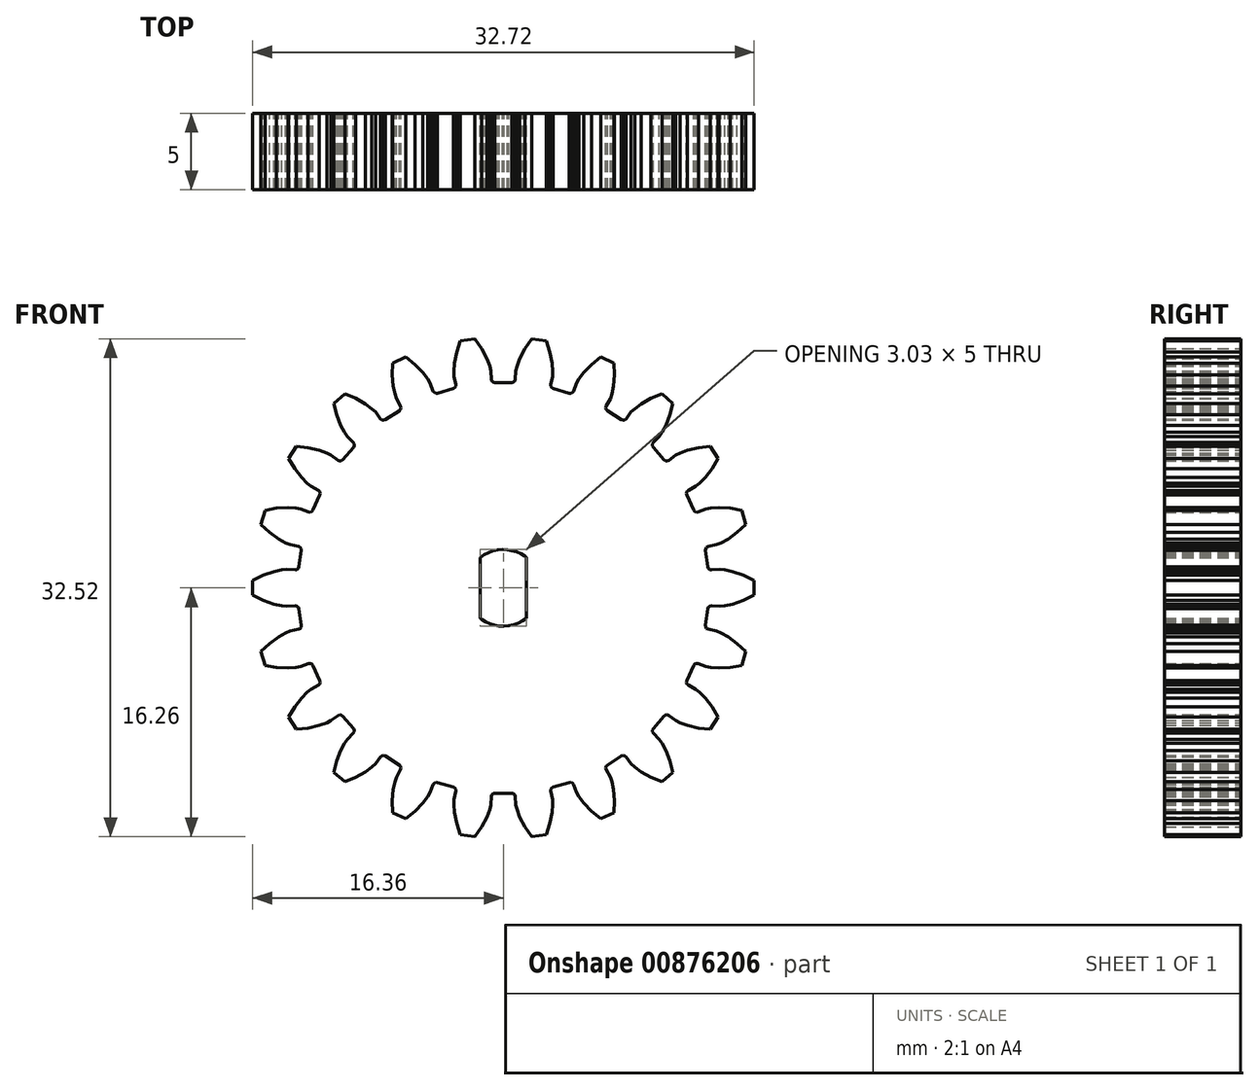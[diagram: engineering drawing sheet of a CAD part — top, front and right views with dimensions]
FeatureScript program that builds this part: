
annotation { "Feature Type Name" : "Feature", "Feature Type Description" : "" }
export const myFeature = defineFeature(function(context is Context, id is Id, definition is map)
    precondition{}
    {
        {
            var Q0;
            Q0=qCreatedBy(makeId("Front.planeOp"),FACE);
            var sketch = newSketch(context, id + "F0", { "sketchPlane" : qUnion([Q0])});
            skLineSegment(sketch, "E0", {"start": v(3.19, -14.67) * mm, "end": v(3.23, -14.15) * mm});
            skLineSegment(sketch, "E1", {"start": v(1.85, 16.26) * mm, "end": v(1.42, 15.62) * mm});
            skLineSegment(sketch, "E2", {"start": v(0.97, -2.3) * mm, "end": v(0.68, -2.4) * mm});
            skLineSegment(sketch, "E3", {"start": v(3.1, 13.28) * mm, "end": v(3.22, 13.83) * mm});
            skLineSegment(sketch, "E4", {"start": v(5.25, 14.06) * mm, "end": v(4.93, 13.65) * mm});
            skLineSegment(sketch, "E5", {"start": v(-9, -12.02) * mm, "end": v(-8.58, -11.7) * mm});
            skLineSegment(sketch, "E6", {"start": v(6.8, -11.58) * mm, "end": v(7.7, -10.99) * mm});
            skLineSegment(sketch, "E7", {"start": v(14.2, -2.94) * mm, "end": v(13.92, -2.82) * mm});
            skLineSegment(sketch, "E8", {"start": v(-0.54, 13.41) * mm, "end": v(-0.65, 13.44) * mm});
            skLineSegment(sketch, "E9", {"start": v(0.54, 13.41) * mm, "end": v(-0.54, 13.41) * mm});
            skLineSegment(sketch, "E10", {"start": v(-0.81, 14.18) * mm, "end": v(-0.89, 14.48) * mm});
            skLineSegment(sketch, "E11", {"start": v(-0.65, 13.44) * mm, "end": v(-0.74, 13.5) * mm});
            skLineSegment(sketch, "E12", {"start": v(-6.71, 11.66) * mm, "end": v(-6.8, 11.58) * mm});
            skLineSegment(sketch, "E13", {"start": v(0.81, 14.18) * mm, "end": v(0.77, 13.61) * mm});
            skLineSegment(sketch, "E14", {"start": v(-9.73, -9.3) * mm, "end": v(-9.73, -9.4) * mm});
            skLineSegment(sketch, "E15", {"start": v(3.1, 13.17) * mm, "end": v(3.1, 13.28) * mm});
            skLineSegment(sketch, "E16", {"start": v(-0.37, 2.47) * mm, "end": v(-0.06, 2.5) * mm});
            skLineSegment(sketch, "E17", {"start": v(0.68, -2.4) * mm, "end": v(0.37, -2.47) * mm});
            skLineSegment(sketch, "E18", {"start": v(4.57, 12.85) * mm, "end": v(4.51, 12.75) * mm});
            skLineSegment(sketch, "E19", {"start": v(0.89, 14.48) * mm, "end": v(0.81, 14.18) * mm});
            skLineSegment(sketch, "E20", {"start": v(1.25, -2.16) * mm, "end": v(0.97, -2.3) * mm});
            skLineSegment(sketch, "E21", {"start": v(-7.23, -14.68) * mm, "end": v(-6.36, -15.08) * mm});
            skLineSegment(sketch, "E22", {"start": v(-8.58, -11.7) * mm, "end": v(-8.35, -11.49) * mm});
            skLineSegment(sketch, "E23", {"start": v(-1.42, 15.62) * mm, "end": v(-1.85, 16.26) * mm});
            skLineSegment(sketch, "E24", {"start": v(0.37, -2.47) * mm, "end": v(0.06, -2.5) * mm});
            skLineSegment(sketch, "E25", {"start": v(-5.25, -14.06) * mm, "end": v(-4.93, -13.65) * mm});
            skLineSegment(sketch, "E26", {"start": v(3.04, 15.4) * mm, "end": v(2.8, 16.12) * mm});
            skLineSegment(sketch, "E27", {"start": v(-0.74, 13.5) * mm, "end": v(-0.77, 13.61) * mm});
            skLineSegment(sketch, "E28", {"start": v(14.07, -5.24) * mm, "end": v(14.8, -5.2) * mm});
            skLineSegment(sketch, "E29", {"start": v(-4.51, -12.75) * mm, "end": v(-4.41, -12.7) * mm});
            skLineSegment(sketch, "E30", {"start": v(-12.06, -6.36) * mm, "end": v(-12.56, -6.63) * mm});
            skLineSegment(sketch, "E31", {"start": v(-13.4, 1.27) * mm, "end": v(-13.48, 1.2) * mm});
            skLineSegment(sketch, "E32", {"start": v(-0.77, 13.61) * mm, "end": v(-0.81, 14.18) * mm});
            skLineSegment(sketch, "E33", {"start": v(-1.08, 14.97) * mm, "end": v(-1.42, 15.62) * mm});
            skLineSegment(sketch, "E34", {"start": v(-8, -11.04) * mm, "end": v(-7.92, -10.97) * mm});
            skLineSegment(sketch, "E35", {"start": v(-6.8, -11.58) * mm, "end": v(-6.71, -11.66) * mm});
            skLineSegment(sketch, "E36", {"start": v(-14.67, 3.2) * mm, "end": v(-14.2, 2.94) * mm});
            skLineSegment(sketch, "E37", {"start": v(-3.19, -14.67) * mm, "end": v(-3.04, -15.4) * mm});
            skLineSegment(sketch, "E38", {"start": v(0.54, -13.41) * mm, "end": v(0.65, -13.44) * mm});
            skLineSegment(sketch, "E39", {"start": v(-15.26, 3.63) * mm, "end": v(-14.67, 3.2) * mm});
            skLineSegment(sketch, "E40", {"start": v(-13.23, 5.15) * mm, "end": v(-13.54, 5.2) * mm});
            skLineSegment(sketch, "E41", {"start": v(-4.93, -13.65) * mm, "end": v(-4.77, -13.37) * mm});
            skLineSegment(sketch, "E42", {"start": v(-12.06, 6.36) * mm, "end": v(-11.98, 6.28) * mm});
            skLineSegment(sketch, "E43", {"start": v(-16.36, 0.48) * mm, "end": v(-16.36, -0.48) * mm});
            skLineSegment(sketch, "E44", {"start": v(-15.67, 0.82) * mm, "end": v(-16.36, 0.48) * mm});
            skLineSegment(sketch, "E45", {"start": v(3.19, 14.67) * mm, "end": v(3.04, 15.4) * mm});
            skLineSegment(sketch, "E46", {"start": v(3.23, 14.15) * mm, "end": v(3.19, 14.67) * mm});
            skLineSegment(sketch, "E47", {"start": v(3.22, 13.83) * mm, "end": v(3.23, 14.15) * mm});
            skLineSegment(sketch, "E48", {"start": v(0.26, 2.49) * mm, "end": v(0.57, 2.43) * mm});
            skLineSegment(sketch, "E49", {"start": v(-0.06, 2.5) * mm, "end": v(0.26, 2.49) * mm});
            skLineSegment(sketch, "E50", {"start": v(-14.02, -8.44) * mm, "end": v(-13.5, -9.25) * mm});
            skLineSegment(sketch, "E51", {"start": v(-13.62, -7.78) * mm, "end": v(-14.02, -8.44) * mm});
            skLineSegment(sketch, "E52", {"start": v(-0.68, 2.4) * mm, "end": v(-0.37, 2.47) * mm});
            skLineSegment(sketch, "E53", {"start": v(-3.16, 13.08) * mm, "end": v(-3.26, 13.02) * mm});
            skLineSegment(sketch, "E54", {"start": v(-3.1, 13.17) * mm, "end": v(-3.16, 13.08) * mm});
            skLineSegment(sketch, "E55", {"start": v(-3.1, 13.28) * mm, "end": v(-3.1, 13.17) * mm});
            skLineSegment(sketch, "E56", {"start": v(-3.22, 13.83) * mm, "end": v(-3.1, 13.28) * mm});
            skLineSegment(sketch, "E57", {"start": v(-3.23, 14.15) * mm, "end": v(-3.22, 13.83) * mm});
            skLineSegment(sketch, "E58", {"start": v(-3.19, 14.67) * mm, "end": v(-3.23, 14.15) * mm});
            skLineSegment(sketch, "E59", {"start": v(-3.04, 15.4) * mm, "end": v(-3.19, 14.67) * mm});
            skLineSegment(sketch, "E60", {"start": v(-2.8, 16.12) * mm, "end": v(-3.04, 15.4) * mm});
            skLineSegment(sketch, "E61", {"start": v(-1.85, 16.26) * mm, "end": v(-2.8, 16.12) * mm});
            skLineSegment(sketch, "E62", {"start": v(5.76, 14.6) * mm, "end": v(5.25, 14.06) * mm});
            skLineSegment(sketch, "E63", {"start": v(6.36, 15.08) * mm, "end": v(5.76, 14.6) * mm});
            skLineSegment(sketch, "E64", {"start": v(7.23, 14.68) * mm, "end": v(6.36, 15.08) * mm});
            skLineSegment(sketch, "E65", {"start": v(-7.2, 13.18) * mm, "end": v(-7.08, 12.66) * mm});
            skLineSegment(sketch, "E66", {"start": v(-7.25, 13.91) * mm, "end": v(-7.2, 13.18) * mm});
            skLineSegment(sketch, "E67", {"start": v(-7.23, 14.68) * mm, "end": v(-7.25, 13.91) * mm});
            skLineSegment(sketch, "E68", {"start": v(-6.36, 15.08) * mm, "end": v(-7.23, 14.68) * mm});
            skLineSegment(sketch, "E69", {"start": v(-5.76, 14.6) * mm, "end": v(-6.36, 15.08) * mm});
            skLineSegment(sketch, "E70", {"start": v(-5.25, 14.06) * mm, "end": v(-5.76, 14.6) * mm});
            skLineSegment(sketch, "E71", {"start": v(-4.93, 13.65) * mm, "end": v(-5.25, 14.06) * mm});
            skLineSegment(sketch, "E72", {"start": v(-4.77, 13.37) * mm, "end": v(-4.93, 13.65) * mm});
            skLineSegment(sketch, "E73", {"start": v(-4.57, 12.85) * mm, "end": v(-4.77, 13.37) * mm});
            skLineSegment(sketch, "E74", {"start": v(-4.51, 12.75) * mm, "end": v(-4.57, 12.85) * mm});
            skLineSegment(sketch, "E75", {"start": v(1.42, 15.62) * mm, "end": v(1.08, 14.97) * mm});
            skLineSegment(sketch, "E76", {"start": v(-13.54, 5.2) * mm, "end": v(-14.07, 5.24) * mm});
            skLineSegment(sketch, "E77", {"start": v(-0.89, 14.48) * mm, "end": v(-1.08, 14.97) * mm});
            skLineSegment(sketch, "E78", {"start": v(13.17, -7.2) * mm, "end": v(12.8, -6.82) * mm});
            skLineSegment(sketch, "E79", {"start": v(2.8, 16.12) * mm, "end": v(1.85, 16.26) * mm});
            skLineSegment(sketch, "E80", {"start": v(-2.8, -16.12) * mm, "end": v(-1.85, -16.26) * mm});
            skLineSegment(sketch, "E81", {"start": v(-11.97, -6.07) * mm, "end": v(-11.95, -6.17) * mm});
            skLineSegment(sketch, "E82", {"start": v(-6.71, -11.87) * mm, "end": v(-6.98, -12.36) * mm});
            skLineSegment(sketch, "E83", {"start": v(-14.46, 1.18) * mm, "end": v(-14.97, 1.07) * mm});
            skLineSegment(sketch, "E84", {"start": v(-14.07, 5.24) * mm, "end": v(-14.8, 5.2) * mm});
            skLineSegment(sketch, "E85", {"start": v(-1.85, -16.26) * mm, "end": v(-1.42, -15.62) * mm});
            skLineSegment(sketch, "E86", {"start": v(-6.36, -15.08) * mm, "end": v(-5.76, -14.6) * mm});
            skLineSegment(sketch, "E87", {"start": v(-4.3, -12.72) * mm, "end": v(-4.41, -12.7) * mm});
            skLineSegment(sketch, "E88", {"start": v(-7.7, -10.99) * mm, "end": v(-7.81, -10.95) * mm});
            skLineSegment(sketch, "E89", {"start": v(7.23, 14.68) * mm, "end": v(7.25, 13.91) * mm});
            skLineSegment(sketch, "E90", {"start": v(0.74, -13.5) * mm, "end": v(0.77, -13.61) * mm});
            skLineSegment(sketch, "E91", {"start": v(-15.56, 5.07) * mm, "end": v(-14.8, 5.2) * mm});
            skLineSegment(sketch, "E92", {"start": v(-3.22, -13.83) * mm, "end": v(-3.23, -14.15) * mm});
            skLineSegment(sketch, "E93", {"start": v(-15.56, 5.07) * mm, "end": v(-15.83, 4.15) * mm});
            skLineSegment(sketch, "E94", {"start": v(-12.8, -6.82) * mm, "end": v(-13.17, -7.2) * mm});
            skLineSegment(sketch, "E95", {"start": v(-13.23, 5.15) * mm, "end": v(-12.7, 4.96) * mm});
            skLineSegment(sketch, "E96", {"start": v(-5.25, -14.06) * mm, "end": v(-5.76, -14.6) * mm});
            skLineSegment(sketch, "E97", {"start": v(-15.26, 3.63) * mm, "end": v(-15.83, 4.15) * mm});
            skLineSegment(sketch, "E98", {"start": v(13.5, -9.25) * mm, "end": v(12.74, -9.16) * mm});
            skLineSegment(sketch, "E99", {"start": v(-13.2, -2.56) * mm, "end": v(-13.27, -2.65) * mm});
            skLineSegment(sketch, "E100", {"start": v(-12.8, -6.82) * mm, "end": v(-12.56, -6.63) * mm});
            skLineSegment(sketch, "E101", {"start": v(-13.48, -1.2) * mm, "end": v(-13.59, -1.18) * mm});
            skLineSegment(sketch, "E102", {"start": v(-3.16, -13.08) * mm, "end": v(-3.1, -13.17) * mm});
            skLineSegment(sketch, "E103", {"start": v(-0.89, -14.48) * mm, "end": v(-1.08, -14.97) * mm});
            skLineSegment(sketch, "E104", {"start": v(11.53, -8.81) * mm, "end": v(11.24, -8.67) * mm});
            skLineSegment(sketch, "E105", {"start": v(-12.02, -9) * mm, "end": v(-12.74, -9.16) * mm});
            skLineSegment(sketch, "E106", {"start": v(-7.81, -10.95) * mm, "end": v(-7.92, -10.97) * mm});
            skLineSegment(sketch, "E107", {"start": v(-0.54, -13.41) * mm, "end": v(-0.65, -13.44) * mm});
            skLineSegment(sketch, "E108", {"start": v(9.64, -12.38) * mm, "end": v(9, -12.02) * mm});
            skLineSegment(sketch, "E109", {"start": v(-3.1, -13.28) * mm, "end": v(-3.22, -13.83) * mm});
            skLineSegment(sketch, "E110", {"start": v(-3.04, -15.4) * mm, "end": v(-2.8, -16.12) * mm});
            skLineSegment(sketch, "E111", {"start": v(-1.5, -2) * mm, "end": v(-1.51, 1.99) * mm});
            skLineSegment(sketch, "E112", {"start": v(-1.42, -2.05) * mm, "end": v(-1.5, -2) * mm});
            skLineSegment(sketch, "E113", {"start": v(-1.16, -2.22) * mm, "end": v(-1.42, -2.05) * mm});
            skLineSegment(sketch, "E114", {"start": v(-1.42, -15.62) * mm, "end": v(-1.08, -14.97) * mm});
            skLineSegment(sketch, "E115", {"start": v(-0.87, -2.34) * mm, "end": v(-1.16, -2.22) * mm});
            skLineSegment(sketch, "E116", {"start": v(-0.89, -14.48) * mm, "end": v(-0.81, -14.18) * mm});
            skLineSegment(sketch, "E117", {"start": v(-0.57, -2.43) * mm, "end": v(-0.87, -2.34) * mm});
            skLineSegment(sketch, "E118", {"start": v(-0.81, -14.18) * mm, "end": v(-0.77, -13.61) * mm});
            skLineSegment(sketch, "E119", {"start": v(-0.77, -13.61) * mm, "end": v(-0.74, -13.5) * mm});
            skLineSegment(sketch, "E120", {"start": v(-0.74, -13.5) * mm, "end": v(-0.65, -13.44) * mm});
            skLineSegment(sketch, "E121", {"start": v(-0.26, -2.49) * mm, "end": v(-0.57, -2.43) * mm});
            skLineSegment(sketch, "E122", {"start": v(-0.54, -13.41) * mm, "end": v(0.54, -13.41) * mm});
            skLineSegment(sketch, "E123", {"start": v(0.06, -2.5) * mm, "end": v(-0.26, -2.49) * mm});
            skLineSegment(sketch, "E124", {"start": v(0.65, -13.44) * mm, "end": v(0.74, -13.5) * mm});
            skLineSegment(sketch, "E125", {"start": v(0.77, -13.61) * mm, "end": v(0.81, -14.18) * mm});
            skLineSegment(sketch, "E126", {"start": v(0.81, -14.18) * mm, "end": v(0.89, -14.48) * mm});
            skLineSegment(sketch, "E127", {"start": v(0.89, -14.48) * mm, "end": v(1.08, -14.97) * mm});
            skLineSegment(sketch, "E128", {"start": v(1.08, -14.97) * mm, "end": v(1.42, -15.62) * mm});
            skLineSegment(sketch, "E129", {"start": v(1.51, -1.99) * mm, "end": v(1.25, -2.16) * mm});
            skLineSegment(sketch, "E130", {"start": v(1.42, -15.62) * mm, "end": v(1.85, -16.26) * mm});
            skLineSegment(sketch, "E131", {"start": v(-15.26, -3.63) * mm, "end": v(-15.83, -4.15) * mm});
            skLineSegment(sketch, "E132", {"start": v(-15.83, -4.15) * mm, "end": v(-15.56, -5.07) * mm});
            skLineSegment(sketch, "E133", {"start": v(-15.56, -5.07) * mm, "end": v(-14.8, -5.2) * mm});
            skLineSegment(sketch, "E134", {"start": v(-14.67, -3.2) * mm, "end": v(-15.26, -3.63) * mm});
            skLineSegment(sketch, "E135", {"start": v(-14.8, -5.2) * mm, "end": v(-14.07, -5.24) * mm});
            skLineSegment(sketch, "E136", {"start": v(-14.2, -2.94) * mm, "end": v(-14.67, -3.2) * mm});
            skLineSegment(sketch, "E137", {"start": v(-13.92, -2.82) * mm, "end": v(-14.2, -2.94) * mm});
            skLineSegment(sketch, "E138", {"start": v(-14.07, -5.24) * mm, "end": v(-13.54, -5.2) * mm});
            skLineSegment(sketch, "E139", {"start": v(-13.37, -2.7) * mm, "end": v(-13.92, -2.82) * mm});
            skLineSegment(sketch, "E140", {"start": v(-13.54, -5.2) * mm, "end": v(-13.23, -5.15) * mm});
            skLineSegment(sketch, "E141", {"start": v(-13.27, -2.65) * mm, "end": v(-13.37, -2.7) * mm});
            skLineSegment(sketch, "E142", {"start": v(-13.23, -5.15) * mm, "end": v(-12.7, -4.96) * mm});
            skLineSegment(sketch, "E143", {"start": v(-13.2, -2.45) * mm, "end": v(-13.2, -2.56) * mm});
            skLineSegment(sketch, "E144", {"start": v(-13.17, -7.2) * mm, "end": v(-13.62, -7.78) * mm});
            skLineSegment(sketch, "E145", {"start": v(-13.5, -9.25) * mm, "end": v(-12.74, -9.16) * mm});
            skLineSegment(sketch, "E146", {"start": v(-11.98, -6.28) * mm, "end": v(-12.06, -6.36) * mm});
            skLineSegment(sketch, "E147", {"start": v(-12.02, -9) * mm, "end": v(-11.53, -8.81) * mm});
            skLineSegment(sketch, "E148", {"start": v(-11.95, -6.17) * mm, "end": v(-11.98, -6.28) * mm});
            skLineSegment(sketch, "E149", {"start": v(-10.88, -11.3) * mm, "end": v(-11.08, -12.05) * mm});
            skLineSegment(sketch, "E150", {"start": v(-11.08, -12.05) * mm, "end": v(-10.35, -12.68) * mm});
            skLineSegment(sketch, "E151", {"start": v(-10.61, -10.62) * mm, "end": v(-10.88, -11.3) * mm});
            skLineSegment(sketch, "E152", {"start": v(-10.36, -10.15) * mm, "end": v(-10.61, -10.62) * mm});
            skLineSegment(sketch, "E153", {"start": v(-10.18, -9.9) * mm, "end": v(-10.36, -10.15) * mm});
            skLineSegment(sketch, "E154", {"start": v(-10.35, -12.68) * mm, "end": v(-9.64, -12.38) * mm});
            skLineSegment(sketch, "E155", {"start": v(-9.79, -9.5) * mm, "end": v(-10.18, -9.9) * mm});
            skLineSegment(sketch, "E156", {"start": v(-9.73, -9.4) * mm, "end": v(-9.79, -9.5) * mm});
            skLineSegment(sketch, "E157", {"start": v(-7.2, -13.18) * mm, "end": v(-7.25, -13.91) * mm});
            skLineSegment(sketch, "E158", {"start": v(-7.25, -13.91) * mm, "end": v(-7.23, -14.68) * mm});
            skLineSegment(sketch, "E159", {"start": v(-7.08, -12.66) * mm, "end": v(-7.2, -13.18) * mm});
            skLineSegment(sketch, "E160", {"start": v(-6.98, -12.36) * mm, "end": v(-7.08, -12.66) * mm});
            skLineSegment(sketch, "E161", {"start": v(-6.69, -11.76) * mm, "end": v(-6.71, -11.87) * mm});
            skLineSegment(sketch, "E162", {"start": v(-3.23, -14.15) * mm, "end": v(-3.19, -14.67) * mm});
            skLineSegment(sketch, "E163", {"start": v(-7.08, 12.66) * mm, "end": v(-6.98, 12.36) * mm});
            skLineSegment(sketch, "E164", {"start": v(-6.98, 12.36) * mm, "end": v(-6.71, 11.87) * mm});
            skLineSegment(sketch, "E165", {"start": v(-6.71, 11.87) * mm, "end": v(-6.69, 11.76) * mm});
            skLineSegment(sketch, "E166", {"start": v(-4.77, -13.37) * mm, "end": v(-4.57, -12.85) * mm});
            skLineSegment(sketch, "E167", {"start": v(-4.57, -12.85) * mm, "end": v(-4.51, -12.75) * mm});
            skLineSegment(sketch, "E168", {"start": v(-4.41, 12.7) * mm, "end": v(-4.51, 12.75) * mm});
            skLineSegment(sketch, "E169", {"start": v(-4.3, 12.72) * mm, "end": v(-4.41, 12.7) * mm});
            skLineSegment(sketch, "E170", {"start": v(-4.3, -12.72) * mm, "end": v(-3.26, -13.02) * mm});
            skLineSegment(sketch, "E171", {"start": v(-3.26, 13.02) * mm, "end": v(-4.3, 12.72) * mm});
            skLineSegment(sketch, "E172", {"start": v(-3.26, -13.02) * mm, "end": v(-3.16, -13.08) * mm});
            skLineSegment(sketch, "E173", {"start": v(-3.1, -13.17) * mm, "end": v(-3.1, -13.28) * mm});
            skLineSegment(sketch, "E174", {"start": v(-10.35, 12.68) * mm, "end": v(-11.08, 12.05) * mm});
            skLineSegment(sketch, "E175", {"start": v(-11.08, 12.05) * mm, "end": v(-10.88, 11.3) * mm});
            skLineSegment(sketch, "E176", {"start": v(-10.88, 11.3) * mm, "end": v(-10.61, 10.62) * mm});
            skLineSegment(sketch, "E177", {"start": v(-10.61, 10.62) * mm, "end": v(-10.36, 10.15) * mm});
            skLineSegment(sketch, "E178", {"start": v(-10.36, 10.15) * mm, "end": v(-10.18, 9.9) * mm});
            skLineSegment(sketch, "E179", {"start": v(-9.64, 12.38) * mm, "end": v(-10.35, 12.68) * mm});
            skLineSegment(sketch, "E180", {"start": v(-10.18, 9.9) * mm, "end": v(-9.79, 9.5) * mm});
            skLineSegment(sketch, "E181", {"start": v(-9.79, 9.5) * mm, "end": v(-9.73, 9.4) * mm});
            skLineSegment(sketch, "E182", {"start": v(-9.73, 9.4) * mm, "end": v(-9.73, 9.3) * mm});
            skLineSegment(sketch, "E183", {"start": v(-9.64, -12.38) * mm, "end": v(-9, -12.02) * mm});
            skLineSegment(sketch, "E184", {"start": v(-9, 12.02) * mm, "end": v(-9.64, 12.38) * mm});
            skLineSegment(sketch, "E185", {"start": v(-8.58, 11.7) * mm, "end": v(-9, 12.02) * mm});
            skLineSegment(sketch, "E186", {"start": v(-8.35, 11.49) * mm, "end": v(-8.58, 11.7) * mm});
            skLineSegment(sketch, "E187", {"start": v(-8.35, -11.49) * mm, "end": v(-8, -11.04) * mm});
            skLineSegment(sketch, "E188", {"start": v(-8, 11.04) * mm, "end": v(-8.35, 11.49) * mm});
            skLineSegment(sketch, "E189", {"start": v(-7.92, 10.97) * mm, "end": v(-8, 11.04) * mm});
            skLineSegment(sketch, "E190", {"start": v(-7.81, 10.95) * mm, "end": v(-7.92, 10.97) * mm});
            skLineSegment(sketch, "E191", {"start": v(-7.7, 10.99) * mm, "end": v(-7.81, 10.95) * mm});
            skLineSegment(sketch, "E192", {"start": v(-7.7, -10.99) * mm, "end": v(-6.8, -11.58) * mm});
            skLineSegment(sketch, "E193", {"start": v(-6.8, 11.58) * mm, "end": v(-7.7, 10.99) * mm});
            skLineSegment(sketch, "E194", {"start": v(-6.71, -11.66) * mm, "end": v(-6.69, -11.76) * mm});
            skLineSegment(sketch, "E195", {"start": v(-6.69, 11.76) * mm, "end": v(-6.71, 11.66) * mm});
            skLineSegment(sketch, "E196", {"start": v(-13.5, 9.25) * mm, "end": v(-14.02, 8.44) * mm});
            skLineSegment(sketch, "E197", {"start": v(-14.02, 8.44) * mm, "end": v(-13.62, 7.78) * mm});
            skLineSegment(sketch, "E198", {"start": v(-13.62, 7.78) * mm, "end": v(-13.17, 7.2) * mm});
            skLineSegment(sketch, "E199", {"start": v(-12.74, 9.16) * mm, "end": v(-13.5, 9.25) * mm});
            skLineSegment(sketch, "E200", {"start": v(-13.17, 7.2) * mm, "end": v(-12.8, 6.82) * mm});
            skLineSegment(sketch, "E201", {"start": v(-12.8, 6.82) * mm, "end": v(-12.56, 6.63) * mm});
            skLineSegment(sketch, "E202", {"start": v(-12.02, 9) * mm, "end": v(-12.74, 9.16) * mm});
            skLineSegment(sketch, "E203", {"start": v(-12.56, 6.63) * mm, "end": v(-12.06, 6.36) * mm});
            skLineSegment(sketch, "E204", {"start": v(-11.53, 8.81) * mm, "end": v(-12.02, 9) * mm});
            skLineSegment(sketch, "E205", {"start": v(-11.98, 6.28) * mm, "end": v(-11.95, 6.17) * mm});
            skLineSegment(sketch, "E206", {"start": v(-11.53, -8.81) * mm, "end": v(-11.24, -8.67) * mm});
            skLineSegment(sketch, "E207", {"start": v(-11.24, 8.67) * mm, "end": v(-11.53, 8.81) * mm});
            skLineSegment(sketch, "E208", {"start": v(-11.24, -8.67) * mm, "end": v(-10.8, -8.33) * mm});
            skLineSegment(sketch, "E209", {"start": v(-10.8, 8.33) * mm, "end": v(-11.24, 8.67) * mm});
            skLineSegment(sketch, "E210", {"start": v(-10.8, -8.33) * mm, "end": v(-10.7, -8.3) * mm});
            skLineSegment(sketch, "E211", {"start": v(-10.7, 8.3) * mm, "end": v(-10.8, 8.33) * mm});
            skLineSegment(sketch, "E212", {"start": v(-10.7, -8.3) * mm, "end": v(-10.58, -8.3) * mm});
            skLineSegment(sketch, "E213", {"start": v(-10.58, 8.3) * mm, "end": v(-10.7, 8.3) * mm});
            skLineSegment(sketch, "E214", {"start": v(-10.58, -8.3) * mm, "end": v(-10.5, -8.37) * mm});
            skLineSegment(sketch, "E215", {"start": v(-10.5, 8.37) * mm, "end": v(-10.58, 8.3) * mm});
            skLineSegment(sketch, "E216", {"start": v(-10.5, -8.37) * mm, "end": v(-9.78, -9.2) * mm});
            skLineSegment(sketch, "E217", {"start": v(-9.78, 9.2) * mm, "end": v(-10.5, 8.37) * mm});
            skLineSegment(sketch, "E218", {"start": v(-9.78, -9.2) * mm, "end": v(-9.73, -9.3) * mm});
            skLineSegment(sketch, "E219", {"start": v(-9.73, 9.3) * mm, "end": v(-9.78, 9.2) * mm});
            skLineSegment(sketch, "E220", {"start": v(-14.2, 2.94) * mm, "end": v(-13.92, 2.82) * mm});
            skLineSegment(sketch, "E221", {"start": v(-13.92, 2.82) * mm, "end": v(-13.37, 2.7) * mm});
            skLineSegment(sketch, "E222", {"start": v(-13.37, 2.7) * mm, "end": v(-13.27, 2.65) * mm});
            skLineSegment(sketch, "E223", {"start": v(-13.27, 2.65) * mm, "end": v(-13.2, 2.56) * mm});
            skLineSegment(sketch, "E224", {"start": v(-13.2, 2.56) * mm, "end": v(-13.2, 2.45) * mm});
            skLineSegment(sketch, "E225", {"start": v(-12.7, -4.96) * mm, "end": v(-12.6, -4.94) * mm});
            skLineSegment(sketch, "E226", {"start": v(-12.6, 4.94) * mm, "end": v(-12.7, 4.96) * mm});
            skLineSegment(sketch, "E227", {"start": v(-12.6, -4.94) * mm, "end": v(-12.5, -4.99) * mm});
            skLineSegment(sketch, "E228", {"start": v(-12.5, 4.99) * mm, "end": v(-12.6, 4.94) * mm});
            skLineSegment(sketch, "E229", {"start": v(-12.5, -4.99) * mm, "end": v(-12.43, -5.08) * mm});
            skLineSegment(sketch, "E230", {"start": v(-12.43, 5.08) * mm, "end": v(-12.5, 4.99) * mm});
            skLineSegment(sketch, "E231", {"start": v(-12.43, -5.08) * mm, "end": v(-11.97, -6.07) * mm});
            skLineSegment(sketch, "E232", {"start": v(-11.97, 6.07) * mm, "end": v(-12.43, 5.08) * mm});
            skLineSegment(sketch, "E233", {"start": v(-11.95, 6.17) * mm, "end": v(-11.97, 6.07) * mm});
            skLineSegment(sketch, "E234", {"start": v(-16.36, -0.48) * mm, "end": v(-15.67, -0.82) * mm});
            skLineSegment(sketch, "E235", {"start": v(-15.67, -0.82) * mm, "end": v(-14.97, -1.07) * mm});
            skLineSegment(sketch, "E236", {"start": v(-14.97, 1.07) * mm, "end": v(-15.67, 0.82) * mm});
            skLineSegment(sketch, "E237", {"start": v(-14.97, -1.07) * mm, "end": v(-14.46, -1.18) * mm});
            skLineSegment(sketch, "E238", {"start": v(-14.46, -1.18) * mm, "end": v(-14.15, -1.22) * mm});
            skLineSegment(sketch, "E239", {"start": v(-14.15, 1.22) * mm, "end": v(-14.46, 1.18) * mm});
            skLineSegment(sketch, "E240", {"start": v(-14.15, -1.22) * mm, "end": v(-13.59, -1.18) * mm});
            skLineSegment(sketch, "E241", {"start": v(-13.59, 1.18) * mm, "end": v(-14.15, 1.22) * mm});
            skLineSegment(sketch, "E242", {"start": v(-13.48, 1.2) * mm, "end": v(-13.59, 1.18) * mm});
            skLineSegment(sketch, "E243", {"start": v(-13.48, -1.2) * mm, "end": v(-13.4, -1.27) * mm});
            skLineSegment(sketch, "E244", {"start": v(-13.4, -1.27) * mm, "end": v(-13.35, -1.37) * mm});
            skLineSegment(sketch, "E245", {"start": v(-13.35, 1.37) * mm, "end": v(-13.4, 1.27) * mm});
            skLineSegment(sketch, "E246", {"start": v(-13.35, -1.37) * mm, "end": v(-13.2, -2.45) * mm});
            skLineSegment(sketch, "E247", {"start": v(-13.2, 2.45) * mm, "end": v(-13.35, 1.37) * mm});
            skLineSegment(sketch, "E248", {"start": v(-1.51, 1.99) * mm, "end": v(-1.25, 2.16) * mm});
            skLineSegment(sketch, "E249", {"start": v(-1.25, 2.16) * mm, "end": v(-0.97, 2.3) * mm});
            skLineSegment(sketch, "E250", {"start": v(-0.97, 2.3) * mm, "end": v(-0.68, 2.4) * mm});
            skLineSegment(sketch, "E251", {"start": v(0.65, 13.44) * mm, "end": v(0.54, 13.41) * mm});
            skLineSegment(sketch, "E252", {"start": v(0.57, 2.43) * mm, "end": v(0.87, 2.34) * mm});
            skLineSegment(sketch, "E253", {"start": v(0.74, 13.5) * mm, "end": v(0.65, 13.44) * mm});
            skLineSegment(sketch, "E254", {"start": v(0.77, 13.61) * mm, "end": v(0.74, 13.5) * mm});
            skLineSegment(sketch, "E255", {"start": v(0.87, 2.34) * mm, "end": v(1.16, 2.22) * mm});
            skLineSegment(sketch, "E256", {"start": v(1.08, 14.97) * mm, "end": v(0.89, 14.48) * mm});
            skLineSegment(sketch, "E257", {"start": v(1.16, 2.22) * mm, "end": v(1.42, 2.05) * mm});
            skLineSegment(sketch, "E258", {"start": v(1.42, 2.05) * mm, "end": v(1.5, 2) * mm});
            skLineSegment(sketch, "E259", {"start": v(1.5, 2) * mm, "end": v(1.51, -1.99) * mm});
            skLineSegment(sketch, "E260", {"start": v(1.85, -16.26) * mm, "end": v(2.8, -16.12) * mm});
            skLineSegment(sketch, "E261", {"start": v(2.8, -16.12) * mm, "end": v(3.04, -15.4) * mm});
            skLineSegment(sketch, "E262", {"start": v(3.04, -15.4) * mm, "end": v(3.19, -14.67) * mm});
            skLineSegment(sketch, "E263", {"start": v(3.22, -13.83) * mm, "end": v(3.1, -13.28) * mm});
            skLineSegment(sketch, "E264", {"start": v(3.23, -14.15) * mm, "end": v(3.22, -13.83) * mm});
            skLineSegment(sketch, "E265", {"start": v(3.1, -13.28) * mm, "end": v(3.1, -13.17) * mm});
            skLineSegment(sketch, "E266", {"start": v(3.1, -13.17) * mm, "end": v(3.16, -13.08) * mm});
            skLineSegment(sketch, "E267", {"start": v(3.16, 13.08) * mm, "end": v(3.1, 13.17) * mm});
            skLineSegment(sketch, "E268", {"start": v(3.16, -13.08) * mm, "end": v(3.26, -13.02) * mm});
            skLineSegment(sketch, "E269", {"start": v(3.26, 13.02) * mm, "end": v(3.16, 13.08) * mm});
            skLineSegment(sketch, "E270", {"start": v(3.26, -13.02) * mm, "end": v(4.3, -12.72) * mm});
            skLineSegment(sketch, "E271", {"start": v(4.3, 12.72) * mm, "end": v(3.26, 13.02) * mm});
            skLineSegment(sketch, "E272", {"start": v(4.3, -12.72) * mm, "end": v(4.41, -12.7) * mm});
            skLineSegment(sketch, "E273", {"start": v(4.41, 12.7) * mm, "end": v(4.3, 12.72) * mm});
            skLineSegment(sketch, "E274", {"start": v(4.41, -12.7) * mm, "end": v(4.51, -12.75) * mm});
            skLineSegment(sketch, "E275", {"start": v(4.51, 12.75) * mm, "end": v(4.41, 12.7) * mm});
            skLineSegment(sketch, "E276", {"start": v(4.51, -12.75) * mm, "end": v(4.57, -12.85) * mm});
            skLineSegment(sketch, "E277", {"start": v(4.57, -12.85) * mm, "end": v(4.77, -13.37) * mm});
            skLineSegment(sketch, "E278", {"start": v(4.77, 13.37) * mm, "end": v(4.57, 12.85) * mm});
            skLineSegment(sketch, "E279", {"start": v(4.77, -13.37) * mm, "end": v(4.93, -13.65) * mm});
            skLineSegment(sketch, "E280", {"start": v(4.93, 13.65) * mm, "end": v(4.77, 13.37) * mm});
            skLineSegment(sketch, "E281", {"start": v(4.93, -13.65) * mm, "end": v(5.25, -14.06) * mm});
            skLineSegment(sketch, "E282", {"start": v(5.25, -14.06) * mm, "end": v(5.76, -14.6) * mm});
            skLineSegment(sketch, "E283", {"start": v(5.76, -14.6) * mm, "end": v(6.36, -15.08) * mm});
            skLineSegment(sketch, "E284", {"start": v(6.36, -15.08) * mm, "end": v(7.23, -14.68) * mm});
            skLineSegment(sketch, "E285", {"start": v(6.71, -11.87) * mm, "end": v(6.69, -11.76) * mm});
            skLineSegment(sketch, "E286", {"start": v(6.98, -12.36) * mm, "end": v(6.71, -11.87) * mm});
            skLineSegment(sketch, "E287", {"start": v(7.08, -12.66) * mm, "end": v(6.98, -12.36) * mm});
            skLineSegment(sketch, "E288", {"start": v(7.2, -13.18) * mm, "end": v(7.08, -12.66) * mm});
            skLineSegment(sketch, "E289", {"start": v(7.23, -14.68) * mm, "end": v(7.25, -13.91) * mm});
            skLineSegment(sketch, "E290", {"start": v(7.25, -13.91) * mm, "end": v(7.2, -13.18) * mm});
            skLineSegment(sketch, "E291", {"start": v(6.69, -11.76) * mm, "end": v(6.71, -11.66) * mm});
            skLineSegment(sketch, "E292", {"start": v(6.71, 11.66) * mm, "end": v(6.69, 11.76) * mm});
            skLineSegment(sketch, "E293", {"start": v(6.71, -11.66) * mm, "end": v(6.8, -11.58) * mm});
            skLineSegment(sketch, "E294", {"start": v(6.8, 11.58) * mm, "end": v(6.71, 11.66) * mm});
            skLineSegment(sketch, "E295", {"start": v(7.7, 10.99) * mm, "end": v(6.8, 11.58) * mm});
            skLineSegment(sketch, "E296", {"start": v(7.7, -10.99) * mm, "end": v(7.81, -10.95) * mm});
            skLineSegment(sketch, "E297", {"start": v(7.81, 10.95) * mm, "end": v(7.7, 10.99) * mm});
            skLineSegment(sketch, "E298", {"start": v(7.81, -10.95) * mm, "end": v(7.92, -10.97) * mm});
            skLineSegment(sketch, "E299", {"start": v(7.92, 10.97) * mm, "end": v(7.81, 10.95) * mm});
            skLineSegment(sketch, "E300", {"start": v(7.92, -10.97) * mm, "end": v(8, -11.04) * mm});
            skLineSegment(sketch, "E301", {"start": v(8, 11.04) * mm, "end": v(7.92, 10.97) * mm});
            skLineSegment(sketch, "E302", {"start": v(8, -11.04) * mm, "end": v(8.35, -11.49) * mm});
            skLineSegment(sketch, "E303", {"start": v(8.35, 11.49) * mm, "end": v(8, 11.04) * mm});
            skLineSegment(sketch, "E304", {"start": v(8.35, -11.49) * mm, "end": v(8.58, -11.7) * mm});
            skLineSegment(sketch, "E305", {"start": v(8.58, 11.7) * mm, "end": v(8.35, 11.49) * mm});
            skLineSegment(sketch, "E306", {"start": v(8.58, -11.7) * mm, "end": v(9, -12.02) * mm});
            skLineSegment(sketch, "E307", {"start": v(9, 12.02) * mm, "end": v(8.58, 11.7) * mm});
            skLineSegment(sketch, "E308", {"start": v(9.64, 12.38) * mm, "end": v(9, 12.02) * mm});
            skLineSegment(sketch, "E309", {"start": v(9.73, -9.4) * mm, "end": v(9.73, -9.3) * mm});
            skLineSegment(sketch, "E310", {"start": v(9.64, -12.38) * mm, "end": v(10.35, -12.68) * mm});
            skLineSegment(sketch, "E311", {"start": v(9.79, -9.5) * mm, "end": v(9.73, -9.4) * mm});
            skLineSegment(sketch, "E312", {"start": v(10.18, -9.9) * mm, "end": v(9.79, -9.5) * mm});
            skLineSegment(sketch, "E313", {"start": v(10.36, -10.15) * mm, "end": v(10.18, -9.9) * mm});
            skLineSegment(sketch, "E314", {"start": v(10.35, -12.68) * mm, "end": v(11.08, -12.05) * mm});
            skLineSegment(sketch, "E315", {"start": v(10.61, -10.62) * mm, "end": v(10.36, -10.15) * mm});
            skLineSegment(sketch, "E316", {"start": v(11.08, -12.05) * mm, "end": v(10.88, -11.3) * mm});
            skLineSegment(sketch, "E317", {"start": v(10.88, -11.3) * mm, "end": v(10.61, -10.62) * mm});
            skLineSegment(sketch, "E318", {"start": v(9.73, -9.3) * mm, "end": v(9.78, -9.2) * mm});
            skLineSegment(sketch, "E319", {"start": v(9.78, 9.2) * mm, "end": v(9.73, 9.3) * mm});
            skLineSegment(sketch, "E320", {"start": v(9.78, -9.2) * mm, "end": v(10.5, -8.37) * mm});
            skLineSegment(sketch, "E321", {"start": v(10.5, 8.37) * mm, "end": v(9.78, 9.2) * mm});
            skLineSegment(sketch, "E322", {"start": v(10.5, -8.37) * mm, "end": v(10.58, -8.3) * mm});
            skLineSegment(sketch, "E323", {"start": v(10.58, 8.3) * mm, "end": v(10.5, 8.37) * mm});
            skLineSegment(sketch, "E324", {"start": v(10.58, -8.3) * mm, "end": v(10.7, -8.3) * mm});
            skLineSegment(sketch, "E325", {"start": v(10.7, 8.3) * mm, "end": v(10.58, 8.3) * mm});
            skLineSegment(sketch, "E326", {"start": v(10.7, -8.3) * mm, "end": v(10.8, -8.33) * mm});
            skLineSegment(sketch, "E327", {"start": v(10.8, 8.33) * mm, "end": v(10.7, 8.3) * mm});
            skLineSegment(sketch, "E328", {"start": v(10.8, -8.33) * mm, "end": v(11.24, -8.67) * mm});
            skLineSegment(sketch, "E329", {"start": v(11.24, 8.67) * mm, "end": v(10.8, 8.33) * mm});
            skLineSegment(sketch, "E330", {"start": v(11.53, 8.81) * mm, "end": v(11.24, 8.67) * mm});
            skLineSegment(sketch, "E331", {"start": v(11.53, -8.81) * mm, "end": v(12.02, -9) * mm});
            skLineSegment(sketch, "E332", {"start": v(11.98, -6.28) * mm, "end": v(11.95, -6.17) * mm});
            skLineSegment(sketch, "E333", {"start": v(12.06, -6.36) * mm, "end": v(11.98, -6.28) * mm});
            skLineSegment(sketch, "E334", {"start": v(12.02, -9) * mm, "end": v(12.74, -9.16) * mm});
            skLineSegment(sketch, "E335", {"start": v(12.56, -6.63) * mm, "end": v(12.06, -6.36) * mm});
            skLineSegment(sketch, "E336", {"start": v(12.8, -6.82) * mm, "end": v(12.56, -6.63) * mm});
            skLineSegment(sketch, "E337", {"start": v(13.62, -7.78) * mm, "end": v(13.17, -7.2) * mm});
            skLineSegment(sketch, "E338", {"start": v(13.5, -9.25) * mm, "end": v(14.02, -8.44) * mm});
            skLineSegment(sketch, "E339", {"start": v(14.02, -8.44) * mm, "end": v(13.62, -7.78) * mm});
            skLineSegment(sketch, "E340", {"start": v(11.95, -6.17) * mm, "end": v(11.97, -6.07) * mm});
            skLineSegment(sketch, "E341", {"start": v(11.97, 6.07) * mm, "end": v(11.95, 6.17) * mm});
            skLineSegment(sketch, "E342", {"start": v(11.97, -6.07) * mm, "end": v(12.43, -5.08) * mm});
            skLineSegment(sketch, "E343", {"start": v(12.43, 5.08) * mm, "end": v(11.97, 6.07) * mm});
            skLineSegment(sketch, "E344", {"start": v(12.43, -5.08) * mm, "end": v(12.5, -4.99) * mm});
            skLineSegment(sketch, "E345", {"start": v(12.5, 4.99) * mm, "end": v(12.43, 5.08) * mm});
            skLineSegment(sketch, "E346", {"start": v(12.5, -4.99) * mm, "end": v(12.6, -4.94) * mm});
            skLineSegment(sketch, "E347", {"start": v(12.6, 4.94) * mm, "end": v(12.5, 4.99) * mm});
            skLineSegment(sketch, "E348", {"start": v(12.6, -4.94) * mm, "end": v(12.7, -4.96) * mm});
            skLineSegment(sketch, "E349", {"start": v(12.7, 4.96) * mm, "end": v(12.6, 4.94) * mm});
            skLineSegment(sketch, "E350", {"start": v(12.7, -4.96) * mm, "end": v(13.23, -5.15) * mm});
            skLineSegment(sketch, "E351", {"start": v(13.2, -2.56) * mm, "end": v(13.2, -2.45) * mm});
            skLineSegment(sketch, "E352", {"start": v(13.27, -2.65) * mm, "end": v(13.2, -2.56) * mm});
            skLineSegment(sketch, "E353", {"start": v(13.23, -5.15) * mm, "end": v(13.54, -5.2) * mm});
            skLineSegment(sketch, "E354", {"start": v(13.37, -2.7) * mm, "end": v(13.27, -2.65) * mm});
            skLineSegment(sketch, "E355", {"start": v(13.92, -2.82) * mm, "end": v(13.37, -2.7) * mm});
            skLineSegment(sketch, "E356", {"start": v(13.54, -5.2) * mm, "end": v(14.07, -5.24) * mm});
            skLineSegment(sketch, "E357", {"start": v(14.67, -3.2) * mm, "end": v(14.2, -2.94) * mm});
            skLineSegment(sketch, "E358", {"start": v(15.26, -3.63) * mm, "end": v(14.67, -3.2) * mm});
            skLineSegment(sketch, "E359", {"start": v(14.8, -5.2) * mm, "end": v(15.56, -5.07) * mm});
            skLineSegment(sketch, "E360", {"start": v(15.56, -5.07) * mm, "end": v(15.83, -4.15) * mm});
            skLineSegment(sketch, "E361", {"start": v(15.83, -4.15) * mm, "end": v(15.26, -3.63) * mm});
            skLineSegment(sketch, "E362", {"start": v(13.2, -2.45) * mm, "end": v(13.35, -1.37) * mm});
            skLineSegment(sketch, "E363", {"start": v(13.35, 1.37) * mm, "end": v(13.2, 2.45) * mm});
            skLineSegment(sketch, "E364", {"start": v(13.35, -1.37) * mm, "end": v(13.4, -1.27) * mm});
            skLineSegment(sketch, "E365", {"start": v(13.4, 1.27) * mm, "end": v(13.35, 1.37) * mm});
            skLineSegment(sketch, "E366", {"start": v(13.4, -1.27) * mm, "end": v(13.48, -1.2) * mm});
            skLineSegment(sketch, "E367", {"start": v(13.48, 1.2) * mm, "end": v(13.4, 1.27) * mm});
            skLineSegment(sketch, "E368", {"start": v(13.59, 1.18) * mm, "end": v(13.48, 1.2) * mm});
            skLineSegment(sketch, "E369", {"start": v(13.48, -1.2) * mm, "end": v(13.59, -1.18) * mm});
            skLineSegment(sketch, "E370", {"start": v(13.59, -1.18) * mm, "end": v(14.15, -1.22) * mm});
            skLineSegment(sketch, "E371", {"start": v(14.15, 1.22) * mm, "end": v(13.59, 1.18) * mm});
            skLineSegment(sketch, "E372", {"start": v(14.46, 1.18) * mm, "end": v(14.15, 1.22) * mm});
            skLineSegment(sketch, "E373", {"start": v(14.15, -1.22) * mm, "end": v(14.46, -1.18) * mm});
            skLineSegment(sketch, "E374", {"start": v(14.46, -1.18) * mm, "end": v(14.97, -1.07) * mm});
            skLineSegment(sketch, "E375", {"start": v(14.97, 1.07) * mm, "end": v(14.46, 1.18) * mm});
            skLineSegment(sketch, "E376", {"start": v(14.97, -1.07) * mm, "end": v(15.67, -0.82) * mm});
            skLineSegment(sketch, "E377", {"start": v(15.67, 0.82) * mm, "end": v(14.97, 1.07) * mm});
            skLineSegment(sketch, "E378", {"start": v(15.67, -0.82) * mm, "end": v(16.36, -0.48) * mm});
            skLineSegment(sketch, "E379", {"start": v(16.36, -0.48) * mm, "end": v(16.36, 0.48) * mm});
            skLineSegment(sketch, "E380", {"start": v(16.36, 0.48) * mm, "end": v(15.67, 0.82) * mm});
            skLineSegment(sketch, "E381", {"start": v(13.23, 5.15) * mm, "end": v(12.7, 4.96) * mm});
            skLineSegment(sketch, "E382", {"start": v(13.2, 2.45) * mm, "end": v(13.2, 2.56) * mm});
            skLineSegment(sketch, "E383", {"start": v(13.2, 2.56) * mm, "end": v(13.27, 2.65) * mm});
            skLineSegment(sketch, "E384", {"start": v(13.54, 5.2) * mm, "end": v(13.23, 5.15) * mm});
            skLineSegment(sketch, "E385", {"start": v(13.27, 2.65) * mm, "end": v(13.37, 2.7) * mm});
            skLineSegment(sketch, "E386", {"start": v(13.37, 2.7) * mm, "end": v(13.92, 2.82) * mm});
            skLineSegment(sketch, "E387", {"start": v(14.07, 5.24) * mm, "end": v(13.54, 5.2) * mm});
            skLineSegment(sketch, "E388", {"start": v(13.92, 2.82) * mm, "end": v(14.2, 2.94) * mm});
            skLineSegment(sketch, "E389", {"start": v(14.8, 5.2) * mm, "end": v(14.07, 5.24) * mm});
            skLineSegment(sketch, "E390", {"start": v(14.2, 2.94) * mm, "end": v(14.67, 3.2) * mm});
            skLineSegment(sketch, "E391", {"start": v(14.67, 3.2) * mm, "end": v(15.26, 3.63) * mm});
            skLineSegment(sketch, "E392", {"start": v(15.56, 5.07) * mm, "end": v(14.8, 5.2) * mm});
            skLineSegment(sketch, "E393", {"start": v(15.26, 3.63) * mm, "end": v(15.83, 4.15) * mm});
            skLineSegment(sketch, "E394", {"start": v(15.83, 4.15) * mm, "end": v(15.56, 5.07) * mm});
            skLineSegment(sketch, "E395", {"start": v(12.02, 9) * mm, "end": v(11.53, 8.81) * mm});
            skLineSegment(sketch, "E396", {"start": v(11.95, 6.17) * mm, "end": v(11.98, 6.28) * mm});
            skLineSegment(sketch, "E397", {"start": v(11.98, 6.28) * mm, "end": v(12.06, 6.36) * mm});
            skLineSegment(sketch, "E398", {"start": v(12.74, 9.16) * mm, "end": v(12.02, 9) * mm});
            skLineSegment(sketch, "E399", {"start": v(12.06, 6.36) * mm, "end": v(12.56, 6.63) * mm});
            skLineSegment(sketch, "E400", {"start": v(12.56, 6.63) * mm, "end": v(12.8, 6.82) * mm});
            skLineSegment(sketch, "E401", {"start": v(13.5, 9.25) * mm, "end": v(12.74, 9.16) * mm});
            skLineSegment(sketch, "E402", {"start": v(12.8, 6.82) * mm, "end": v(13.17, 7.2) * mm});
            skLineSegment(sketch, "E403", {"start": v(13.17, 7.2) * mm, "end": v(13.62, 7.78) * mm});
            skLineSegment(sketch, "E404", {"start": v(13.62, 7.78) * mm, "end": v(14.02, 8.44) * mm});
            skLineSegment(sketch, "E405", {"start": v(14.02, 8.44) * mm, "end": v(13.5, 9.25) * mm});
            skLineSegment(sketch, "E406", {"start": v(10.35, 12.68) * mm, "end": v(9.64, 12.38) * mm});
            skLineSegment(sketch, "E407", {"start": v(9.73, 9.3) * mm, "end": v(9.73, 9.4) * mm});
            skLineSegment(sketch, "E408", {"start": v(9.73, 9.4) * mm, "end": v(9.79, 9.5) * mm});
            skLineSegment(sketch, "E409", {"start": v(9.79, 9.5) * mm, "end": v(10.18, 9.9) * mm});
            skLineSegment(sketch, "E410", {"start": v(10.18, 9.9) * mm, "end": v(10.36, 10.15) * mm});
            skLineSegment(sketch, "E411", {"start": v(11.08, 12.05) * mm, "end": v(10.35, 12.68) * mm});
            skLineSegment(sketch, "E412", {"start": v(10.36, 10.15) * mm, "end": v(10.61, 10.62) * mm});
            skLineSegment(sketch, "E413", {"start": v(10.61, 10.62) * mm, "end": v(10.88, 11.3) * mm});
            skLineSegment(sketch, "E414", {"start": v(10.88, 11.3) * mm, "end": v(11.08, 12.05) * mm});
            skLineSegment(sketch, "E415", {"start": v(6.69, 11.76) * mm, "end": v(6.71, 11.87) * mm});
            skLineSegment(sketch, "E416", {"start": v(6.71, 11.87) * mm, "end": v(6.98, 12.36) * mm});
            skLineSegment(sketch, "E417", {"start": v(6.98, 12.36) * mm, "end": v(7.08, 12.66) * mm});
            skLineSegment(sketch, "E418", {"start": v(7.08, 12.66) * mm, "end": v(7.2, 13.18) * mm});
            skLineSegment(sketch, "E419", {"start": v(7.2, 13.18) * mm, "end": v(7.25, 13.91) * mm});
            skSolve(sketch);
        }
        {
            var Q0;
            Q0 = qSketchRegion(id + "F0", true);
            extrude(context, id + "F1", {"entities" : qUnion([Q0]), "depth" : 5 * mm, "offsetDistance" : 25 * mm});
        }
    });
